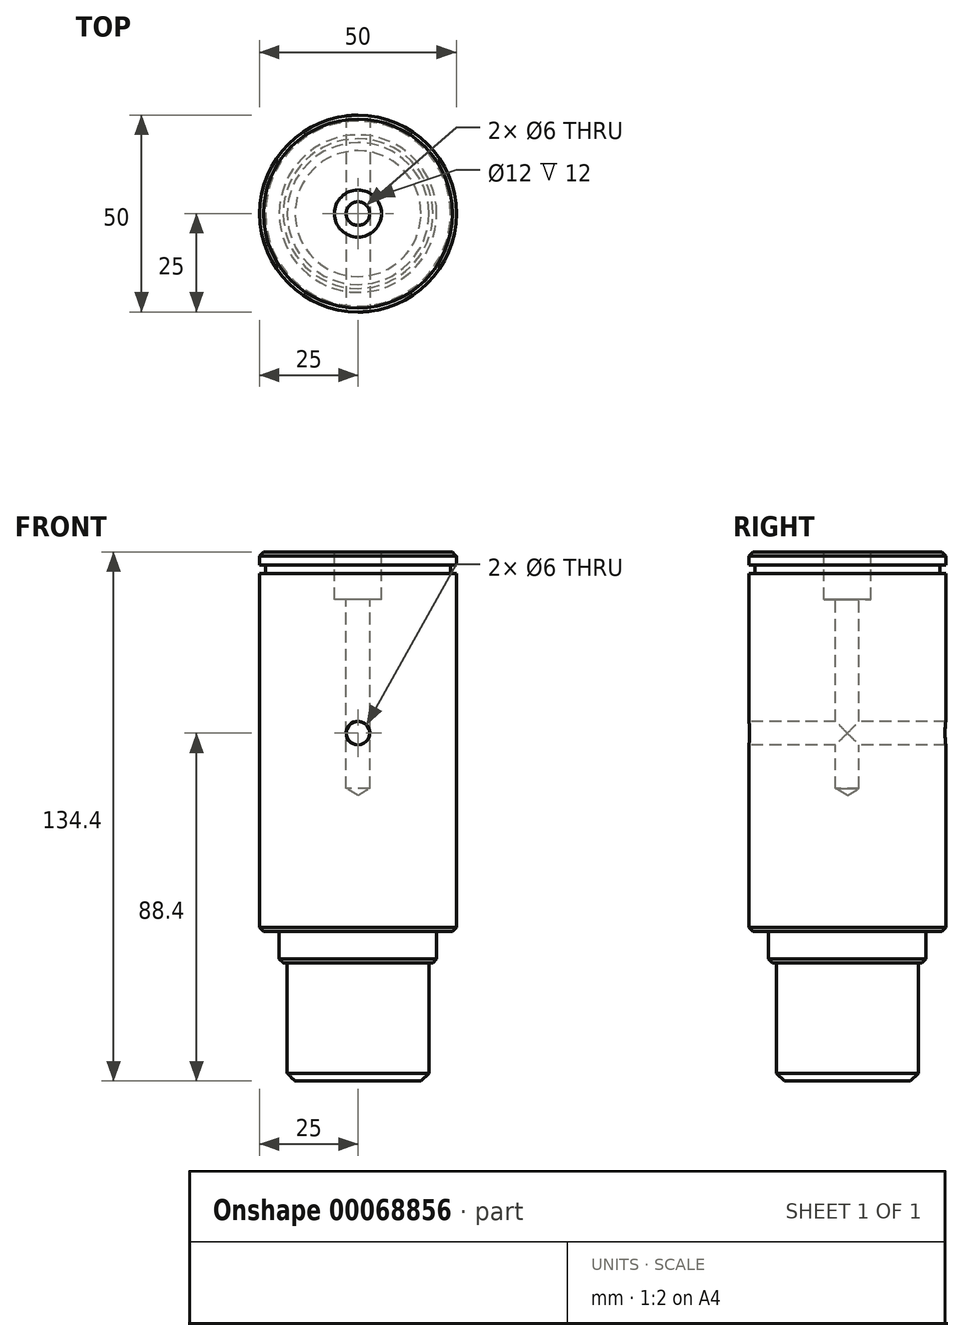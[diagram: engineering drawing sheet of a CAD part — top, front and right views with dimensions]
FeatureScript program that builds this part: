
annotation { "Feature Type Name" : "Feature", "Feature Type Description" : "" }
export const myFeature = defineFeature(function(context is Context, id is Id, definition is map)
    precondition{}
    {
        {
            var Q0;
            Q0=qCreatedBy(makeId("Top.planeOp"),FACE);
            var sketch = newSketch(context, id + "F0", { "sketchPlane" : qUnion([Q0])});
            skCircle(sketch, "E0", {"center": v(0, 0) * mm, "radius": 25 * mm});
            skSolve(sketch);
        }
        {
            var Q0;
            Q0 = qSketchRegion(id + "F0", true);
            extrude(context, id + "F1", {"entities" : qUnion([Q0]), "depth" : 91 * mm});
        }
        {
            var Q0;
            Q0=makeQuery(id+"F1.opExtrude","CAP_FACE",FACE,{"disambiguationData":[OSD([sQuery(id+"F0.wireOp",EDGE,"E0")])],"isStart":false});
            var sketch = newSketch(context, id + "F2", { "sketchPlane" : qUnion([Q0])});
            skCircle(sketch, "E1", {"center": v(0, 0) * mm, "radius": 23.5 * mm});
            skSolve(sketch);
        }
        {
            var Q0;
            Q0 = qSketchRegion(id + "F2", true);
            extrude(context, id + "F3", {"entities" : qUnion([Q0]), "operationType" : NewBodyOperationType.ADD, "depth" : 2.15 * mm});
        }
        {
            var Q0;
            Q0=makeQuery(id+"F3.opExtrude","CAP_FACE",FACE,{"disambiguationData":[OSD([sQuery(id+"F2.wireOp",EDGE,"E1")])],"isStart":false});
            var sketch = newSketch(context, id + "F4", { "sketchPlane" : qUnion([Q0])});
            skCircle(sketch, "E2", {"center": v(0, 0) * mm, "radius": 25 * mm});
            skSolve(sketch);
        }
        {
            var Q0;
            Q0 = qSketchRegion(id + "F4", true);
            extrude(context, id + "F5", {"entities" : qUnion([Q0]), "operationType" : NewBodyOperationType.ADD, "depth" : 3.25 * mm});
        }
        {
            var Q0;
            Q0=makeQuery(id+"F5.opExtrude","CAP_FACE",FACE,{"disambiguationData":[OSD([sQuery(id+"F4.wireOp",EDGE,"E2")])],"isStart":false});
            chamfer(context, id + "F6", {"entities" : qUnion([Q0]), "width" : 1 * mm, "tangentPropagation" : true});
        }
        {
            var Q0;
            Q0=makeQuery(id+"F1.opExtrude","CAP_FACE",FACE,{"disambiguationData":[OSD([sQuery(id+"F0.wireOp",EDGE,"E0")])],"isStart":true});
            var sketch = newSketch(context, id + "F7", { "sketchPlane" : qUnion([Q0])});
            skCircle(sketch, "E3", {"center": v(0, 0) * mm, "radius": 20 * mm});
            skSolve(sketch);
        }
        {
            var Q0;
            Q0 = qSketchRegion(id + "F7", true);
            extrude(context, id + "F8", {"entities" : qUnion([Q0]), "operationType" : NewBodyOperationType.ADD, "depth" : 8 * mm});
        }
        {
            var Q0;
            Q0=makeQuery(id+"F8.opExtrude","CAP_FACE",FACE,{"disambiguationData":[OSD([sQuery(id+"F7.wireOp",EDGE,"E3")])],"isStart":false});
            var sketch = newSketch(context, id + "F9", { "sketchPlane" : qUnion([Q0])});
            skCircle(sketch, "E4", {"center": v(0, 0) * mm, "radius": 18 * mm});
            skSolve(sketch);
        }
        {
            var Q0;
            Q0 = qSketchRegion(id + "F9", true);
            extrude(context, id + "F10", {"entities" : qUnion([Q0]), "operationType" : NewBodyOperationType.ADD, "depth" : 30 * mm});
        }
        {
            var Q0;
            Q0=makeQuery(id+"F1.opExtrude","CAP_EDGE",EDGE,{"disambiguationData":[OSD([sQuery(id+"F0.wireOp",EDGE,"E0")])],"isStart":true});
            var Q1;
            Q1=makeQuery(id+"F8.opExtrude","CAP_EDGE",EDGE,{"disambiguationData":[OSD([sQuery(id+"F7.wireOp",EDGE,"E3")])],"isStart":false});
            chamfer(context, id + "F11", {"entities" : qUnion([Q0, Q1]), "width" : 1 * mm, "tangentPropagation" : true});
        }
        {
            var Q0;
            Q0=makeQuery(id+"F10.opExtrude","CAP_FACE",FACE,{"disambiguationData":[OSD([sQuery(id+"F9.wireOp",EDGE,"E4")])],"isStart":false});
            chamfer(context, id + "F12", {"entities" : qUnion([Q0]), "width" : 2 * mm, "tangentPropagation" : true});
        }
        {
            var Q0;
            Q0=makeQuery(id+"F5.opExtrude","CAP_FACE",FACE,{"disambiguationData":[OSD([sQuery(id+"F4.wireOp",EDGE,"E2")])],"isStart":false});
            var sketch = newSketch(context, id + "F13", { "sketchPlane" : qUnion([Q0])});
            skPoint(sketch, "E5", {"position": v(0, 0) * mm});
            skSolve(sketch);
        }
        {
            var Q0;
            Q0=sQuery(id+"F13.wireOp",VERTEX,"E5");
            var Q1;
            Q1=makeQuery(id+"F1.opExtrude","SWEPT_BODY",BODY,{"disambiguationData":[OSD([sQuery(id+"F0.wireOp",EDGE,"E0")])]});
            hole(context, id + "F14", {"style" : HoleStyle.C_BORE, "holeDiameter" : 6 * mm, "cBoreDiameter" : 12 * mm, "cBoreDepth" : 12 * mm, "endStyle" : HoleEndStyle.BLIND, "holeDepth" : 60 * mm, "locations" : qUnion([Q0]), "scope" : qUnion([Q1])});
        }
        {
            var Q0;
            Q0=qCreatedBy(makeId("Front.planeOp"),FACE);
            cPlane(context, id + "F15", {"entities" : qUnion([Q0]), "cplaneType" : CPlaneType.OFFSET, "offset" : 25 * mm, "width" : 150 * mm, "height" : 150 * mm});
        }
        {
            var Q0;
            Q0=qCreatedBy(id+"F15.planeOp",FACE);
            var sketch = newSketch(context, id + "F16", { "sketchPlane" : qUnion([Q0])});
            skLineSegment(sketch, "E6.0", {"start": v(-24, 96.4) * mm, "end": v(24, 96.4) * mm, "construction": true});
            skLineSegment(sketch, "E7.0", {"start": v(-24, 50.4) * mm, "end": v(24, 50.4) * mm, "construction": true});
            skLineSegment(sketch, "E8", {"start": v(0, -73.76) * mm, "end": v(0, 107.2) * mm, "construction": true});
            skPoint(sketch, "E9", {"position": v(0, 50.4) * mm});
            skSolve(sketch);
        }
        {
            var Q0;
            Q0=sQuery(id+"F16.wireOp",VERTEX,"E9");
            var Q1;
            Q1=makeQuery(id+"F1.opExtrude","SWEPT_BODY",BODY,{"disambiguationData":[OSD([sQuery(id+"F0.wireOp",EDGE,"E0")])]});
            hole(context, id + "F17", {"style" : HoleStyle.SIMPLE, "holeDiameter" : 6 * mm, "endStyle" : HoleEndStyle.THROUGH, "locations" : qUnion([Q0]), "scope" : qUnion([Q1])});
        }
    });
